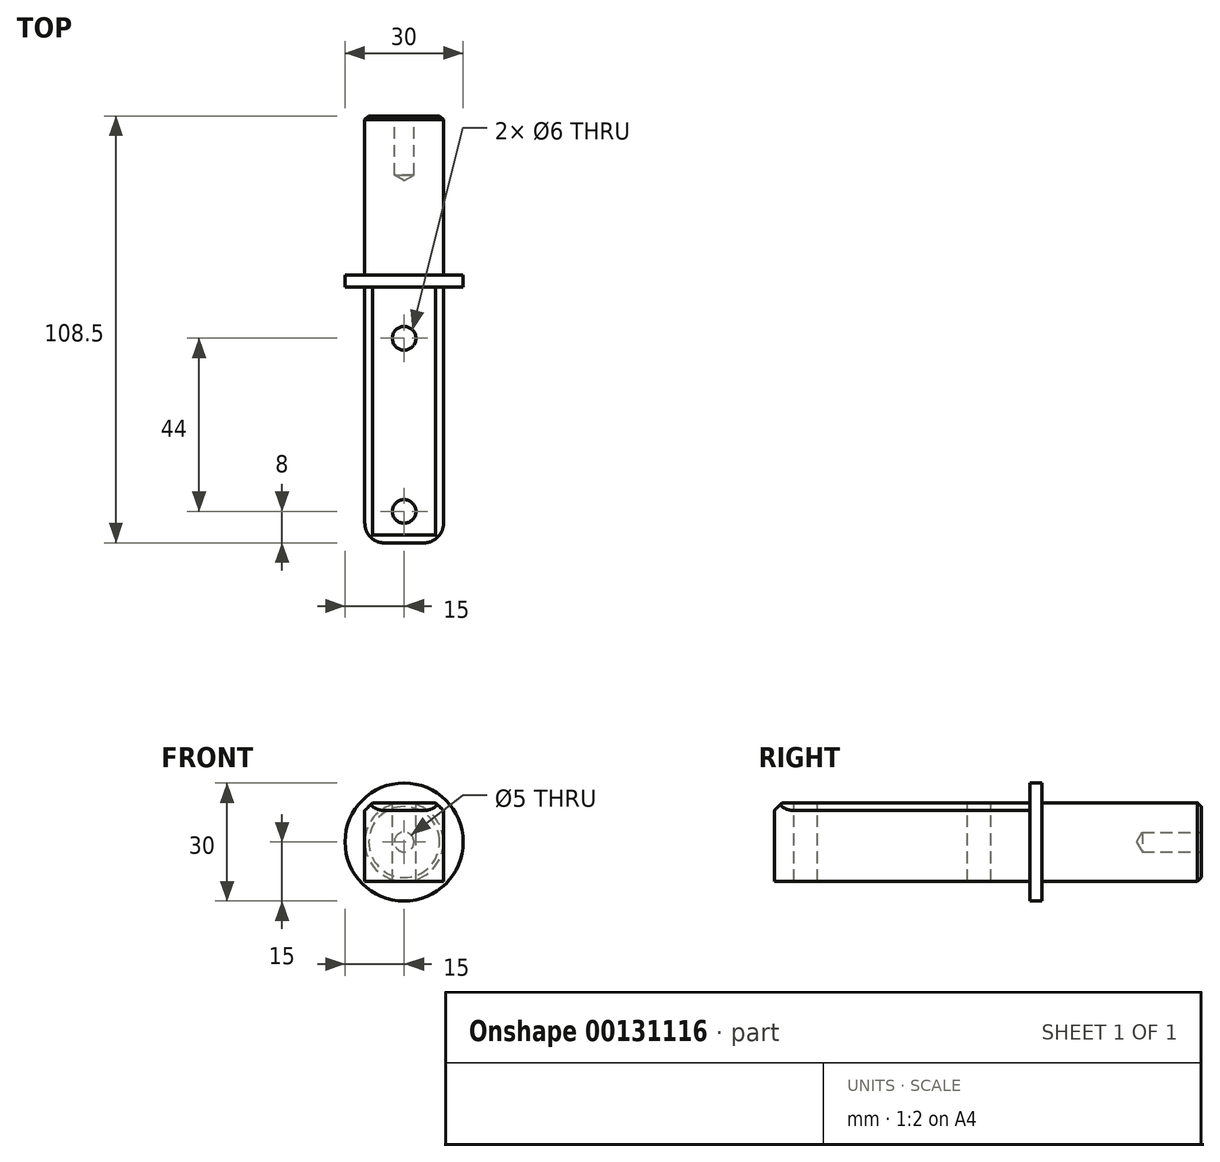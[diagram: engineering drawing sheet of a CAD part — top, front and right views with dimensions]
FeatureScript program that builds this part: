
annotation { "Feature Type Name" : "Feature", "Feature Type Description" : "" }
export const myFeature = defineFeature(function(context is Context, id is Id, definition is map)
    precondition{}
    {
        {
            var Q0;
            Q0=qCreatedBy(makeId("Front.planeOp"),FACE);
            var sketch = newSketch(context, id + "F0", { "sketchPlane" : qUnion([Q0])});
            skCircle(sketch, "E0", {"center": v(0, 0) * mm, "radius": 15 * mm});
            skLineSegment(sketch, "E1.bottom", {"start": v(10, -10) * mm, "end": v(-10, -10) * mm});
            skLineSegment(sketch, "E1.top", {"start": v(10, 10) * mm, "end": v(-10, 10) * mm});
            skLineSegment(sketch, "E1.left", {"start": v(10, -10) * mm, "end": v(10, 10) * mm});
            skLineSegment(sketch, "E1.right", {"start": v(-10, -10) * mm, "end": v(-10, 10) * mm});
            skSolve(sketch);
        }
        {
            var Q0;
            Q0=makeQuery(id+"F0.imprint","IMPRINT",FACE,{"disambiguationData":[TD([[makeQuery(id+"F0.imprint","IMPRINT",EDGE,{"derivedFrom":sQuery(id+"F0.wireOp",EDGE,"E1.bottom")}),-1.0]])]});
            extrude(context, id + "F1", {"entities" : qUnion([Q0]), "depth" : 65 * mm});
        }
        {
            var Q0;
            Q0=makeQuery(id+"F0.imprint","IMPRINT",FACE,{"disambiguationData":[TD([[makeQuery(id+"F0.imprint","IMPRINT",EDGE,{"derivedFrom":sQuery(id+"F0.wireOp",EDGE,"E1.bottom")}),-1.0]])]});
            var Q1;
            Q1=makeQuery(id+"F0.imprint","IMPRINT",FACE,{"disambiguationData":[TD([[makeQuery(id+"F0.imprint","IMPRINT",EDGE,{"derivedFrom":sQuery(id+"F0.wireOp",EDGE,"E0")}),1.0]])]});
            var Q2;
            Q2=makeQuery(id+"F1.opExtrude","CAP_FACE",FACE,{"disambiguationData":[OSD([sQuery(id+"F0.wireOp",EDGE,"E1.bottom"),sQuery(id+"F0.wireOp",EDGE,"E1.top"),sQuery(id+"F0.wireOp",EDGE,"E1.left"),sQuery(id+"F0.wireOp",EDGE,"E1.right")])],"isStart":true});
            extrude(context, id + "F2", {"entities" : qUnion([Q0, Q1, Q2]), "operationType" : NewBodyOperationType.ADD, "oppositeDirection" : true, "depth" : 3 * mm});
        }
        {
            var Q0;
            Q0=makeQuery(id+"F2.opExtrude","CAP_FACE",FACE,{"disambiguationData":[OSD([sQuery(id+"F0.wireOp",EDGE,"E0")])],"isStart":false});
            var sketch = newSketch(context, id + "F3", { "sketchPlane" : qUnion([Q0])});
            skCircle(sketch, "E2", {"center": v(0, 0) * mm, "radius": 10 * mm});
            skSolve(sketch);
        }
        {
            var Q0;
            Q0=makeQuery(id+"F3.imprint","IMPRINT",FACE,{"disambiguationData":[TD([[makeQuery(id+"F3.imprint","IMPRINT",EDGE,{"derivedFrom":sQuery(id+"F3.wireOp",EDGE,"E2")}),1.0]])]});
            extrude(context, id + "F4", {"entities" : qUnion([Q0]), "operationType" : NewBodyOperationType.ADD, "depth" : 40.5 * mm});
        }
        {
            var Q0;
            Q0=makeQuery(id+"F4.opExtrude","CAP_FACE",FACE,{"disambiguationData":[OSD([sQuery(id+"F3.wireOp",EDGE,"E2")])],"isStart":false});
            var sketch = newSketch(context, id + "F5", { "sketchPlane" : qUnion([Q0])});
            skPoint(sketch, "E3", {"position": v(0, 0) * mm});
            skSolve(sketch);
        }
        {
            var Q0;
            Q0=sQuery(id+"F5.wireOp",VERTEX,"E3");
            var Q1;
            Q1=makeQuery(id+"F1.opExtrude","SWEPT_BODY",BODY,{"disambiguationData":[OSD([sQuery(id+"F0.wireOp",EDGE,"E1.bottom"),sQuery(id+"F0.wireOp",EDGE,"E1.top"),sQuery(id+"F0.wireOp",EDGE,"E1.left"),sQuery(id+"F0.wireOp",EDGE,"E1.right")])]});
            hole(context, id + "F6", {"style" : HoleStyle.SIMPLE, "endStyle" : HoleEndStyle.BLIND, "holeDiameter" : 5 * mm, "holeDepth" : 15 * mm, "locations" : qUnion([Q0]), "scope" : qUnion([Q1])});
        }
        {
            var Q0;
            Q0=makeQuery(id+"F4.opExtrude","CAP_EDGE",EDGE,{"disambiguationData":[OSD([sQuery(id+"F3.wireOp",EDGE,"E2")])],"isStart":false});
            chamfer(context, id + "F7", {"entities" : qUnion([Q0]), "width" : 1 * mm, "tangentPropagation" : true});
        }
        {
            var Q0;
            Q0=makeQuery(id+"F1.opExtrude","SWEPT_FACE",FACE,{"disambiguationData":[OSD([sQuery(id+"F0.wireOp",EDGE,"E1.top")])]});
            var sketch = newSketch(context, id + "F8", { "sketchPlane" : qUnion([Q0])});
            skPoint(sketch, "E4", {"position": v(0, -57) * mm});
            skPoint(sketch, "E5", {"position": v(0, -13) * mm});
            skSolve(sketch);
        }
        {
            var Q0;
            Q0=sQuery(id+"F8.wireOp",VERTEX,"E5");
            var Q1;
            Q1=sQuery(id+"F8.wireOp",VERTEX,"E4");
            var Q2;
            Q2=makeQuery(id+"F1.opExtrude","SWEPT_BODY",BODY,{"disambiguationData":[OSD([sQuery(id+"F0.wireOp",EDGE,"E1.bottom"),sQuery(id+"F0.wireOp",EDGE,"E1.top"),sQuery(id+"F0.wireOp",EDGE,"E1.left"),sQuery(id+"F0.wireOp",EDGE,"E1.right")])]});
            hole(context, id + "F9", {"style" : HoleStyle.SIMPLE, "endStyle" : HoleEndStyle.THROUGH, "holeDiameter" : 6 * mm, "locations" : qUnion([Q0, Q1]), "scope" : qUnion([Q2]), "isTappedThrough" : true});
        }
        {
            var Q0;
            Q0=makeQuery(id+"F1.opExtrude","CAP_EDGE",EDGE,{"disambiguationData":[OSD([sQuery(id+"F0.wireOp",EDGE,"E1.top")])],"isStart":false});
            var Q1;
            Q1=makeQuery(id+"F1.opExtrude","SWEPT_EDGE",EDGE,{"disambiguationData":[OSD([sQuery(id+"F0.wireOp",EDGE,"E1.top"),sQuery(id+"F0.wireOp",EDGE,"E1.right")])]});
            var Q2;
            Q2=makeQuery(id+"F1.opExtrude","SWEPT_EDGE",EDGE,{"disambiguationData":[OSD([sQuery(id+"F0.wireOp",EDGE,"E1.top"),sQuery(id+"F0.wireOp",EDGE,"E1.left")])]});
            chamfer(context, id + "F10", {"entities" : qUnion([Q0, Q1, Q2]), "width" : 2 * mm, "tangentPropagation" : true});
        }
        {
            var Q0;
            Q0=makeQuery(id+"F1.opExtrude","CAP_EDGE",EDGE,{"disambiguationData":[OSD([sQuery(id+"F0.wireOp",EDGE,"E1.right")])],"isStart":false});
            var Q1;
            Q1=makeQuery(id+"F1.opExtrude","CAP_EDGE",EDGE,{"disambiguationData":[OSD([sQuery(id+"F0.wireOp",EDGE,"E1.left")])],"isStart":false});
            fillet(context, id + "F11", {"entities" : qUnion([Q0, Q1]), "radius" : 5 * mm, "tangentPropagation" : true, "allowEdgeOverflow" : false});
        }
    });
